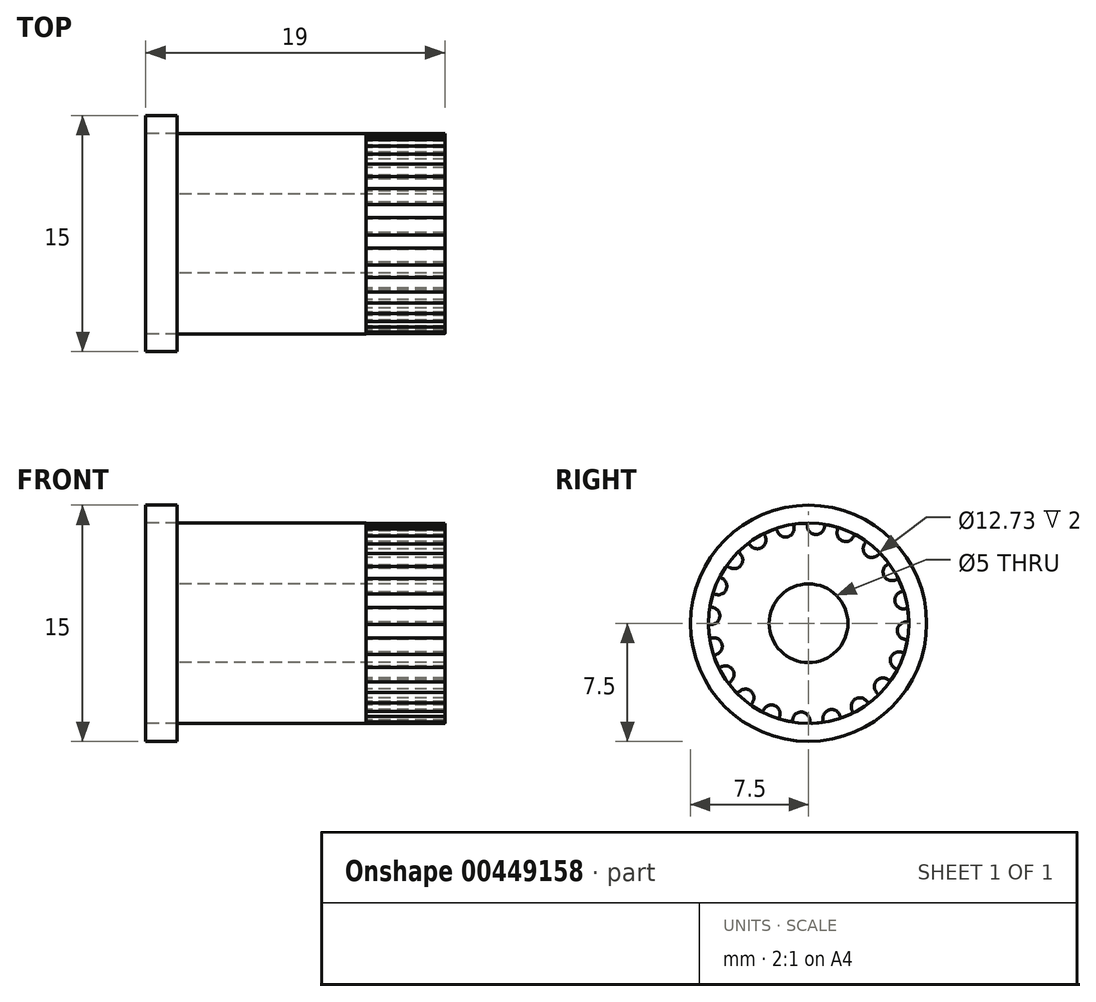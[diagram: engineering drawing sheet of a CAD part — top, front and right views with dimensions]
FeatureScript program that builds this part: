
annotation { "Feature Type Name" : "Feature", "Feature Type Description" : "" }
export const myFeature = defineFeature(function(context is Context, id is Id, definition is map)
    precondition{}
    {
        {
            var Q0;
            Q0=qCreatedBy(makeId("Front.planeOp"),FACE);
            var sketch = newSketch(context, id + "F0", { "sketchPlane" : qUnion([Q0])});
            skLineSegment(sketch, "E0", {"start": v(0, 0) * mm, "end": v(62.27, 0) * mm, "construction": true});
            skLineSegment(sketch, "E1.bottom", {"start": v(0, 2.5) * mm, "end": v(2, 2.5) * mm});
            skLineSegment(sketch, "E1.top", {"start": v(0, 7.5) * mm, "end": v(2, 7.5) * mm});
            skLineSegment(sketch, "E1.left", {"start": v(0, 2.5) * mm, "end": v(0, 7.5) * mm});
            skLineSegment(sketch, "E1.right", {"start": v(2, 2.5) * mm, "end": v(2, 7.5) * mm});
            skLineSegment(sketch, "E2.bottom", {"start": v(0, 6.37) * mm, "end": v(14, 6.37) * mm});
            skLineSegment(sketch, "E2.top", {"start": v(0, 2.5) * mm, "end": v(14, 2.5) * mm});
            skLineSegment(sketch, "E2.left", {"start": v(0, 6.37) * mm, "end": v(0, 2.5) * mm});
            skLineSegment(sketch, "E2.right", {"start": v(14, 6.37) * mm, "end": v(14, 2.5) * mm});
            skLineSegment(sketch, "E3.MirrorCS", {"start": v(14, -6.37) * mm, "end": v(14, -2.5) * mm});
            skLineSegment(sketch, "E4.MirrorCS", {"start": v(0, -6.37) * mm, "end": v(0, -2.5) * mm});
            skLineSegment(sketch, "E5.MirrorCS", {"start": v(0, -2.5) * mm, "end": v(2, -2.5) * mm});
            skLineSegment(sketch, "E6.MirrorCS", {"start": v(0, -2.5) * mm, "end": v(14, -2.5) * mm});
            skLineSegment(sketch, "E7.MirrorCS", {"start": v(0, -7.5) * mm, "end": v(2, -7.5) * mm});
            skLineSegment(sketch, "E8.MirrorCS", {"start": v(0, -2.5) * mm, "end": v(0, -7.5) * mm});
            skLineSegment(sketch, "E9.MirrorCS", {"start": v(0, -6.37) * mm, "end": v(14, -6.37) * mm});
            skLineSegment(sketch, "E10.MirrorCS", {"start": v(2, -2.5) * mm, "end": v(2, -7.5) * mm});
            skSolve(sketch);
        }
        {
            var Q0;
            {var subQ5=sQuery(id+"F0.wireOp",EDGE,"E2.right");Q0=makeQuery(id+"F0.imprint","IMPRINT",FACE,{"disambiguationData":[TD([[makeQuery(id+"F0.imprint","IMPRINT",EDGE,{"derivedFrom":subQ5}),-1.0]])]});}
            var Q1;
            {var subQ5=sQuery(id+"F0.wireOp",EDGE,"E2.left");Q1=makeQuery(id+"F0.imprint","IMPRINT",FACE,{"disambiguationData":[TD([[makeQuery(id+"F0.imprint","IMPRINT",EDGE,{"derivedFrom":subQ5}),1.0]])]});}
            var Q2;
            {var subQ0=sQuery(id+"F0.wireOp",EDGE,"E1.top");Q2=makeQuery(id+"F0.imprint","IMPRINT",FACE,{"disambiguationData":[TD([[makeQuery(id+"F0.imprint","IMPRINT",EDGE,{"derivedFrom":subQ0}),-1.0]])]});}
            var Q3;
            Q3=sQuery(id+"F0.wireOp",EDGE,"E0");
            revolve(context, id + "F1", {"entities" : qUnion([Q0, Q1, Q2]), "axis" : qUnion([Q3]), "revolveType" : RevolveType.FULL});
        }
        {
            var Q0;
            Q0=makeQuery(id+"F1.opRevolve","SWEPT_FACE",FACE,{"disambiguationData":[OSD([sQuery(id+"F0.wireOp",EDGE,"E2.right")])]});
            var sketch = newSketch(context, id + "F2", { "sketchPlane" : qUnion([Q0])});
            skLineSegment(sketch, "E11", {"start": v(0.48, 6.35) * mm, "end": v(0, 0) * mm, "construction": true});
            skArc(sketch, "E12", {"start": v(0.43, 5.64) * mm, "mid": v(0.82, 5.76) * mm, "end": v(1.02, 6.12) * mm});
            skArc(sketch, "E13", {"start": v(1.84, 5.93) * mm, "mid": v(1.86, 5.52) * mm, "end": v(2.15, 5.23) * mm});
            skLineSegment(sketch, "E14", {"start": v(1.02, 6.13) * mm, "end": v(1.02, 6.12) * mm});
            skLineSegment(sketch, "E15", {"start": v(1.84, 5.94) * mm, "end": v(1.84, 5.93) * mm});
            skLineSegment(sketch, "E16", {"start": v(1.19, 6.25) * mm, "end": v(1.74, 6.11) * mm});
            skArc(sketch, "E17.filletArc", {"start": v(1.19, 6.25) * mm, "mid": v(1.08, 6.23) * mm, "end": v(1.02, 6.13) * mm});
            skArc(sketch, "E18.filletArc", {"start": v(1.84, 5.94) * mm, "mid": v(1.83, 6.05) * mm, "end": v(1.74, 6.11) * mm});
            skArc(sketch, "E19.1.0", {"start": v(-1.34, 5.5) * mm, "mid": v(-1, 5.73) * mm, "end": v(-0.93, 6.14) * mm});
            skLineSegment(sketch, "E19.1.1", {"start": v(-0.93, 6.15) * mm, "end": v(-0.93, 6.14) * mm});
            skArc(sketch, "E19.1.2", {"start": v(-0.8, 6.3) * mm, "mid": v(-0.9, 6.25) * mm, "end": v(-0.93, 6.15) * mm});
            skLineSegment(sketch, "E19.1.3", {"start": v(-0.8, 6.3) * mm, "end": v(-0.23, 6.35) * mm});
            skArc(sketch, "E19.1.4", {"start": v(-0.08, 6.22) * mm, "mid": v(-0.13, 6.32) * mm, "end": v(-0.23, 6.35) * mm});
            skLineSegment(sketch, "E19.1.5", {"start": v(-0.08, 6.22) * mm, "end": v(-0.08, 6.2) * mm});
            skArc(sketch, "E19.1.6", {"start": v(-0.08, 6.2) * mm, "mid": v(0.06, 5.82) * mm, "end": v(0.43, 5.64) * mm});
            skArc(sketch, "E19.2.0", {"start": v(-2.97, 4.81) * mm, "mid": v(-2.73, 5.14) * mm, "end": v(-2.78, 5.55) * mm});
            skLineSegment(sketch, "E19.2.1", {"start": v(-2.78, 5.56) * mm, "end": v(-2.78, 5.55) * mm});
            skArc(sketch, "E19.2.2", {"start": v(-2.71, 5.75) * mm, "mid": v(-2.79, 5.67) * mm, "end": v(-2.78, 5.56) * mm});
            skLineSegment(sketch, "E19.2.3", {"start": v(-2.71, 5.75) * mm, "end": v(-2.18, 5.97) * mm});
            skArc(sketch, "E19.2.4", {"start": v(-2, 5.89) * mm, "mid": v(-2.07, 5.97) * mm, "end": v(-2.18, 5.97) * mm});
            skLineSegment(sketch, "E19.2.5", {"start": v(-2, 5.89) * mm, "end": v(-2, 5.88) * mm});
            skArc(sketch, "E19.2.6", {"start": v(-2, 5.88) * mm, "mid": v(-1.74, 5.55) * mm, "end": v(-1.34, 5.5) * mm});
            skPoint(sketch, "E19.center", {"position": v(0, 0) * mm});
            skArc(sketch, "E20.2.3.0", {"start": v(-4.31, 3.66) * mm, "mid": v(-4.18, 4.05) * mm, "end": v(-4.36, 4.42) * mm});
            skLineSegment(sketch, "E20.4.3.0", {"start": v(-4.36, 4.43) * mm, "end": v(-4.36, 4.42) * mm});
            skArc(sketch, "E20.7.3.0", {"start": v(-4.35, 4.63) * mm, "mid": v(-4.4, 4.53) * mm, "end": v(-4.36, 4.43) * mm});
            skLineSegment(sketch, "E20.11.3.0", {"start": v(-4.35, 4.63) * mm, "end": v(-3.92, 5) * mm});
            skArc(sketch, "E20.14.3.0", {"start": v(-3.72, 4.98) * mm, "mid": v(-3.82, 5.04) * mm, "end": v(-3.92, 5) * mm});
            skLineSegment(sketch, "E20.18.3.0", {"start": v(-3.72, 4.98) * mm, "end": v(-3.71, 4.97) * mm});
            skArc(sketch, "E20.21.3.0", {"start": v(-3.71, 4.97) * mm, "mid": v(-3.37, 4.74) * mm, "end": v(-2.97, 4.81) * mm});
            skArc(sketch, "E20.2.4.0", {"start": v(-5.23, 2.15) * mm, "mid": v(-5.23, 2.56) * mm, "end": v(-5.5, 2.86) * mm});
            skLineSegment(sketch, "E20.4.4.0", {"start": v(-5.52, 2.86) * mm, "end": v(-5.5, 2.86) * mm});
            skArc(sketch, "E20.7.4.0", {"start": v(-5.57, 3.06) * mm, "mid": v(-5.59, 2.95) * mm, "end": v(-5.52, 2.86) * mm});
            skLineSegment(sketch, "E20.11.4.0", {"start": v(-5.57, 3.06) * mm, "end": v(-5.28, 3.55) * mm});
            skArc(sketch, "E20.14.4.0", {"start": v(-5.08, 3.59) * mm, "mid": v(-5.19, 3.61) * mm, "end": v(-5.28, 3.55) * mm});
            skLineSegment(sketch, "E20.18.4.0", {"start": v(-5.08, 3.59) * mm, "end": v(-5.07, 3.58) * mm});
            skArc(sketch, "E20.21.4.0", {"start": v(-5.07, 3.58) * mm, "mid": v(-4.67, 3.47) * mm, "end": v(-4.31, 3.66) * mm});
            skArc(sketch, "E20.2.5.0", {"start": v(-5.64, 0.43) * mm, "mid": v(-5.76, 0.82) * mm, "end": v(-6.12, 1.02) * mm});
            skLineSegment(sketch, "E20.4.5.0", {"start": v(-6.13, 1.02) * mm, "end": v(-6.12, 1.02) * mm});
            skArc(sketch, "E20.7.5.0", {"start": v(-6.25, 1.19) * mm, "mid": v(-6.23, 1.08) * mm, "end": v(-6.13, 1.02) * mm});
            skLineSegment(sketch, "E20.11.5.0", {"start": v(-6.25, 1.19) * mm, "end": v(-6.11, 1.74) * mm});
            skArc(sketch, "E20.14.5.0", {"start": v(-5.94, 1.84) * mm, "mid": v(-6.05, 1.83) * mm, "end": v(-6.11, 1.74) * mm});
            skLineSegment(sketch, "E20.18.5.0", {"start": v(-5.94, 1.84) * mm, "end": v(-5.93, 1.84) * mm});
            skArc(sketch, "E20.21.5.0", {"start": v(-5.93, 1.84) * mm, "mid": v(-5.52, 1.86) * mm, "end": v(-5.23, 2.15) * mm});
            skArc(sketch, "E20.2.6.0", {"start": v(-5.5, -1.34) * mm, "mid": v(-5.73, -1) * mm, "end": v(-6.14, -0.93) * mm});
            skLineSegment(sketch, "E20.4.6.0", {"start": v(-6.15, -0.93) * mm, "end": v(-6.14, -0.93) * mm});
            skArc(sketch, "E20.7.6.0", {"start": v(-6.3, -0.8) * mm, "mid": v(-6.25, -0.9) * mm, "end": v(-6.15, -0.93) * mm});
            skLineSegment(sketch, "E20.11.6.0", {"start": v(-6.3, -0.8) * mm, "end": v(-6.35, -0.23) * mm});
            skArc(sketch, "E20.14.6.0", {"start": v(-6.22, -0.08) * mm, "mid": v(-6.32, -0.13) * mm, "end": v(-6.35, -0.23) * mm});
            skLineSegment(sketch, "E20.18.6.0", {"start": v(-6.22, -0.08) * mm, "end": v(-6.2, -0.08) * mm});
            skArc(sketch, "E20.21.6.0", {"start": v(-6.2, -0.08) * mm, "mid": v(-5.82, 0.06) * mm, "end": v(-5.64, 0.43) * mm});
            skArc(sketch, "E20.2.7.0", {"start": v(-4.81, -2.97) * mm, "mid": v(-5.14, -2.73) * mm, "end": v(-5.55, -2.78) * mm});
            skLineSegment(sketch, "E20.4.7.0", {"start": v(-5.56, -2.78) * mm, "end": v(-5.55, -2.78) * mm});
            skArc(sketch, "E20.7.7.0", {"start": v(-5.75, -2.71) * mm, "mid": v(-5.67, -2.79) * mm, "end": v(-5.56, -2.78) * mm});
            skLineSegment(sketch, "E20.11.7.0", {"start": v(-5.75, -2.71) * mm, "end": v(-5.97, -2.18) * mm});
            skArc(sketch, "E20.14.7.0", {"start": v(-5.89, -2) * mm, "mid": v(-5.97, -2.07) * mm, "end": v(-5.97, -2.18) * mm});
            skLineSegment(sketch, "E20.18.7.0", {"start": v(-5.89, -2) * mm, "end": v(-5.88, -2) * mm});
            skArc(sketch, "E20.21.7.0", {"start": v(-5.88, -2) * mm, "mid": v(-5.55, -1.74) * mm, "end": v(-5.5, -1.34) * mm});
            skArc(sketch, "E20.2.8.0", {"start": v(-3.66, -4.31) * mm, "mid": v(-4.05, -4.18) * mm, "end": v(-4.42, -4.36) * mm});
            skLineSegment(sketch, "E20.4.8.0", {"start": v(-4.43, -4.36) * mm, "end": v(-4.42, -4.36) * mm});
            skArc(sketch, "E20.7.8.0", {"start": v(-4.63, -4.35) * mm, "mid": v(-4.53, -4.4) * mm, "end": v(-4.43, -4.36) * mm});
            skLineSegment(sketch, "E20.11.8.0", {"start": v(-4.63, -4.35) * mm, "end": v(-5, -3.92) * mm});
            skArc(sketch, "E20.14.8.0", {"start": v(-4.98, -3.72) * mm, "mid": v(-5.04, -3.82) * mm, "end": v(-5, -3.92) * mm});
            skLineSegment(sketch, "E20.18.8.0", {"start": v(-4.98, -3.72) * mm, "end": v(-4.97, -3.71) * mm});
            skArc(sketch, "E20.21.8.0", {"start": v(-4.97, -3.71) * mm, "mid": v(-4.74, -3.37) * mm, "end": v(-4.81, -2.97) * mm});
            skArc(sketch, "E20.2.9.0", {"start": v(-2.15, -5.23) * mm, "mid": v(-2.56, -5.23) * mm, "end": v(-2.86, -5.5) * mm});
            skLineSegment(sketch, "E20.4.9.0", {"start": v(-2.86, -5.52) * mm, "end": v(-2.86, -5.5) * mm});
            skArc(sketch, "E20.7.9.0", {"start": v(-3.06, -5.57) * mm, "mid": v(-2.95, -5.59) * mm, "end": v(-2.86, -5.52) * mm});
            skLineSegment(sketch, "E20.11.9.0", {"start": v(-3.06, -5.57) * mm, "end": v(-3.55, -5.28) * mm});
            skArc(sketch, "E20.14.9.0", {"start": v(-3.59, -5.08) * mm, "mid": v(-3.61, -5.19) * mm, "end": v(-3.55, -5.28) * mm});
            skLineSegment(sketch, "E20.18.9.0", {"start": v(-3.59, -5.08) * mm, "end": v(-3.58, -5.07) * mm});
            skArc(sketch, "E20.21.9.0", {"start": v(-3.58, -5.07) * mm, "mid": v(-3.47, -4.67) * mm, "end": v(-3.66, -4.31) * mm});
            skArc(sketch, "E20.2.10.0", {"start": v(-0.43, -5.64) * mm, "mid": v(-0.82, -5.76) * mm, "end": v(-1.02, -6.12) * mm});
            skLineSegment(sketch, "E20.4.10.0", {"start": v(-1.02, -6.13) * mm, "end": v(-1.02, -6.12) * mm});
            skArc(sketch, "E20.7.10.0", {"start": v(-1.19, -6.25) * mm, "mid": v(-1.08, -6.23) * mm, "end": v(-1.02, -6.13) * mm});
            skLineSegment(sketch, "E20.11.10.0", {"start": v(-1.19, -6.25) * mm, "end": v(-1.74, -6.11) * mm});
            skArc(sketch, "E20.14.10.0", {"start": v(-1.84, -5.94) * mm, "mid": v(-1.83, -6.05) * mm, "end": v(-1.74, -6.11) * mm});
            skLineSegment(sketch, "E20.18.10.0", {"start": v(-1.84, -5.94) * mm, "end": v(-1.84, -5.93) * mm});
            skArc(sketch, "E20.21.10.0", {"start": v(-1.84, -5.93) * mm, "mid": v(-1.86, -5.52) * mm, "end": v(-2.15, -5.23) * mm});
            skArc(sketch, "E20.2.11.0", {"start": v(1.34, -5.5) * mm, "mid": v(1, -5.73) * mm, "end": v(0.93, -6.14) * mm});
            skLineSegment(sketch, "E20.4.11.0", {"start": v(0.93, -6.15) * mm, "end": v(0.93, -6.14) * mm});
            skArc(sketch, "E20.7.11.0", {"start": v(0.8, -6.3) * mm, "mid": v(0.9, -6.25) * mm, "end": v(0.93, -6.15) * mm});
            skLineSegment(sketch, "E20.11.11.0", {"start": v(0.8, -6.3) * mm, "end": v(0.23, -6.35) * mm});
            skArc(sketch, "E20.14.11.0", {"start": v(0.08, -6.22) * mm, "mid": v(0.13, -6.32) * mm, "end": v(0.23, -6.35) * mm});
            skLineSegment(sketch, "E20.18.11.0", {"start": v(0.08, -6.22) * mm, "end": v(0.08, -6.2) * mm});
            skArc(sketch, "E20.21.11.0", {"start": v(0.08, -6.2) * mm, "mid": v(-0.06, -5.82) * mm, "end": v(-0.43, -5.64) * mm});
            skArc(sketch, "E20.2.12.0", {"start": v(2.97, -4.81) * mm, "mid": v(2.73, -5.14) * mm, "end": v(2.78, -5.55) * mm});
            skLineSegment(sketch, "E20.4.12.0", {"start": v(2.78, -5.56) * mm, "end": v(2.78, -5.55) * mm});
            skArc(sketch, "E20.7.12.0", {"start": v(2.71, -5.75) * mm, "mid": v(2.79, -5.67) * mm, "end": v(2.78, -5.56) * mm});
            skLineSegment(sketch, "E20.11.12.0", {"start": v(2.71, -5.75) * mm, "end": v(2.18, -5.97) * mm});
            skArc(sketch, "E20.14.12.0", {"start": v(2, -5.89) * mm, "mid": v(2.07, -5.97) * mm, "end": v(2.18, -5.97) * mm});
            skLineSegment(sketch, "E20.18.12.0", {"start": v(2, -5.89) * mm, "end": v(2, -5.88) * mm});
            skArc(sketch, "E20.21.12.0", {"start": v(2, -5.88) * mm, "mid": v(1.74, -5.55) * mm, "end": v(1.34, -5.5) * mm});
            skArc(sketch, "E20.2.13.0", {"start": v(4.31, -3.66) * mm, "mid": v(4.18, -4.05) * mm, "end": v(4.36, -4.42) * mm});
            skLineSegment(sketch, "E20.4.13.0", {"start": v(4.36, -4.43) * mm, "end": v(4.36, -4.42) * mm});
            skArc(sketch, "E20.7.13.0", {"start": v(4.35, -4.63) * mm, "mid": v(4.4, -4.53) * mm, "end": v(4.36, -4.43) * mm});
            skLineSegment(sketch, "E20.11.13.0", {"start": v(4.35, -4.63) * mm, "end": v(3.92, -5) * mm});
            skArc(sketch, "E20.14.13.0", {"start": v(3.72, -4.98) * mm, "mid": v(3.82, -5.04) * mm, "end": v(3.92, -5) * mm});
            skLineSegment(sketch, "E20.18.13.0", {"start": v(3.72, -4.98) * mm, "end": v(3.71, -4.97) * mm});
            skArc(sketch, "E20.21.13.0", {"start": v(3.71, -4.97) * mm, "mid": v(3.37, -4.74) * mm, "end": v(2.97, -4.81) * mm});
            skArc(sketch, "E20.2.14.0", {"start": v(5.23, -2.15) * mm, "mid": v(5.23, -2.56) * mm, "end": v(5.5, -2.86) * mm});
            skLineSegment(sketch, "E20.4.14.0", {"start": v(5.52, -2.86) * mm, "end": v(5.5, -2.86) * mm});
            skArc(sketch, "E20.7.14.0", {"start": v(5.57, -3.06) * mm, "mid": v(5.59, -2.95) * mm, "end": v(5.52, -2.86) * mm});
            skLineSegment(sketch, "E20.11.14.0", {"start": v(5.57, -3.06) * mm, "end": v(5.28, -3.55) * mm});
            skArc(sketch, "E20.14.14.0", {"start": v(5.08, -3.59) * mm, "mid": v(5.19, -3.61) * mm, "end": v(5.28, -3.55) * mm});
            skLineSegment(sketch, "E20.18.14.0", {"start": v(5.08, -3.59) * mm, "end": v(5.07, -3.58) * mm});
            skArc(sketch, "E20.21.14.0", {"start": v(5.07, -3.58) * mm, "mid": v(4.67, -3.47) * mm, "end": v(4.31, -3.66) * mm});
            skArc(sketch, "E20.2.15.0", {"start": v(5.64, -0.43) * mm, "mid": v(5.76, -0.82) * mm, "end": v(6.12, -1.02) * mm});
            skLineSegment(sketch, "E20.4.15.0", {"start": v(6.13, -1.02) * mm, "end": v(6.12, -1.02) * mm});
            skArc(sketch, "E20.7.15.0", {"start": v(6.25, -1.19) * mm, "mid": v(6.23, -1.08) * mm, "end": v(6.13, -1.02) * mm});
            skLineSegment(sketch, "E20.11.15.0", {"start": v(6.25, -1.19) * mm, "end": v(6.11, -1.74) * mm});
            skArc(sketch, "E20.14.15.0", {"start": v(5.94, -1.84) * mm, "mid": v(6.05, -1.83) * mm, "end": v(6.11, -1.74) * mm});
            skLineSegment(sketch, "E20.18.15.0", {"start": v(5.94, -1.84) * mm, "end": v(5.93, -1.84) * mm});
            skArc(sketch, "E20.21.15.0", {"start": v(5.93, -1.84) * mm, "mid": v(5.52, -1.86) * mm, "end": v(5.23, -2.15) * mm});
            skArc(sketch, "E20.2.16.0", {"start": v(5.5, 1.34) * mm, "mid": v(5.73, 1) * mm, "end": v(6.14, 0.93) * mm});
            skLineSegment(sketch, "E20.4.16.0", {"start": v(6.15, 0.93) * mm, "end": v(6.14, 0.93) * mm});
            skArc(sketch, "E20.7.16.0", {"start": v(6.3, 0.8) * mm, "mid": v(6.25, 0.9) * mm, "end": v(6.15, 0.93) * mm});
            skLineSegment(sketch, "E20.11.16.0", {"start": v(6.3, 0.8) * mm, "end": v(6.35, 0.23) * mm});
            skArc(sketch, "E20.14.16.0", {"start": v(6.22, 0.08) * mm, "mid": v(6.32, 0.13) * mm, "end": v(6.35, 0.23) * mm});
            skLineSegment(sketch, "E20.18.16.0", {"start": v(6.22, 0.08) * mm, "end": v(6.2, 0.08) * mm});
            skArc(sketch, "E20.21.16.0", {"start": v(6.2, 0.08) * mm, "mid": v(5.82, -0.06) * mm, "end": v(5.64, -0.43) * mm});
            skArc(sketch, "E20.2.17.0", {"start": v(4.81, 2.97) * mm, "mid": v(5.14, 2.73) * mm, "end": v(5.55, 2.78) * mm});
            skLineSegment(sketch, "E20.4.17.0", {"start": v(5.56, 2.78) * mm, "end": v(5.55, 2.78) * mm});
            skArc(sketch, "E20.7.17.0", {"start": v(5.75, 2.71) * mm, "mid": v(5.67, 2.79) * mm, "end": v(5.56, 2.78) * mm});
            skLineSegment(sketch, "E20.11.17.0", {"start": v(5.75, 2.71) * mm, "end": v(5.97, 2.18) * mm});
            skArc(sketch, "E20.14.17.0", {"start": v(5.89, 2) * mm, "mid": v(5.97, 2.07) * mm, "end": v(5.97, 2.18) * mm});
            skLineSegment(sketch, "E20.18.17.0", {"start": v(5.89, 2) * mm, "end": v(5.88, 2) * mm});
            skArc(sketch, "E20.21.17.0", {"start": v(5.88, 2) * mm, "mid": v(5.55, 1.74) * mm, "end": v(5.5, 1.34) * mm});
            skArc(sketch, "E20.2.18.0", {"start": v(3.66, 4.31) * mm, "mid": v(4.05, 4.18) * mm, "end": v(4.42, 4.36) * mm});
            skLineSegment(sketch, "E20.4.18.0", {"start": v(4.43, 4.36) * mm, "end": v(4.42, 4.36) * mm});
            skArc(sketch, "E20.7.18.0", {"start": v(4.63, 4.35) * mm, "mid": v(4.53, 4.4) * mm, "end": v(4.43, 4.36) * mm});
            skLineSegment(sketch, "E20.11.18.0", {"start": v(4.63, 4.35) * mm, "end": v(5, 3.92) * mm});
            skArc(sketch, "E20.14.18.0", {"start": v(4.98, 3.72) * mm, "mid": v(5.04, 3.82) * mm, "end": v(5, 3.92) * mm});
            skLineSegment(sketch, "E20.18.18.0", {"start": v(4.98, 3.72) * mm, "end": v(4.97, 3.71) * mm});
            skArc(sketch, "E20.21.18.0", {"start": v(4.97, 3.71) * mm, "mid": v(4.74, 3.37) * mm, "end": v(4.81, 2.97) * mm});
            skArc(sketch, "E20.2.19.0", {"start": v(2.15, 5.23) * mm, "mid": v(2.56, 5.23) * mm, "end": v(2.86, 5.5) * mm});
            skLineSegment(sketch, "E20.4.19.0", {"start": v(2.86, 5.52) * mm, "end": v(2.86, 5.5) * mm});
            skArc(sketch, "E20.7.19.0", {"start": v(3.06, 5.57) * mm, "mid": v(2.95, 5.59) * mm, "end": v(2.86, 5.52) * mm});
            skLineSegment(sketch, "E20.11.19.0", {"start": v(3.06, 5.57) * mm, "end": v(3.55, 5.28) * mm});
            skArc(sketch, "E20.14.19.0", {"start": v(3.59, 5.08) * mm, "mid": v(3.61, 5.19) * mm, "end": v(3.55, 5.28) * mm});
            skLineSegment(sketch, "E20.18.19.0", {"start": v(3.59, 5.08) * mm, "end": v(3.58, 5.07) * mm});
            skArc(sketch, "E20.21.19.0", {"start": v(3.58, 5.07) * mm, "mid": v(3.47, 4.67) * mm, "end": v(3.66, 4.31) * mm});
            skSolve(sketch);
        }
        {
            var Q0;
            Q0=makeQuery(id+"F2.imprint","IMPRINT",FACE,{"disambiguationData":[TD([[makeQuery(id+"F2.imprint","IMPRINT",EDGE,{"derivedFrom":sQuery(id+"F2.wireOp",EDGE,"E12")}),-1.0]])]});
            extrude(context, id + "F3", {"entities" : qUnion([Q0]), "operationType" : NewBodyOperationType.ADD, "depth" : 5 * mm});
        }
    });
